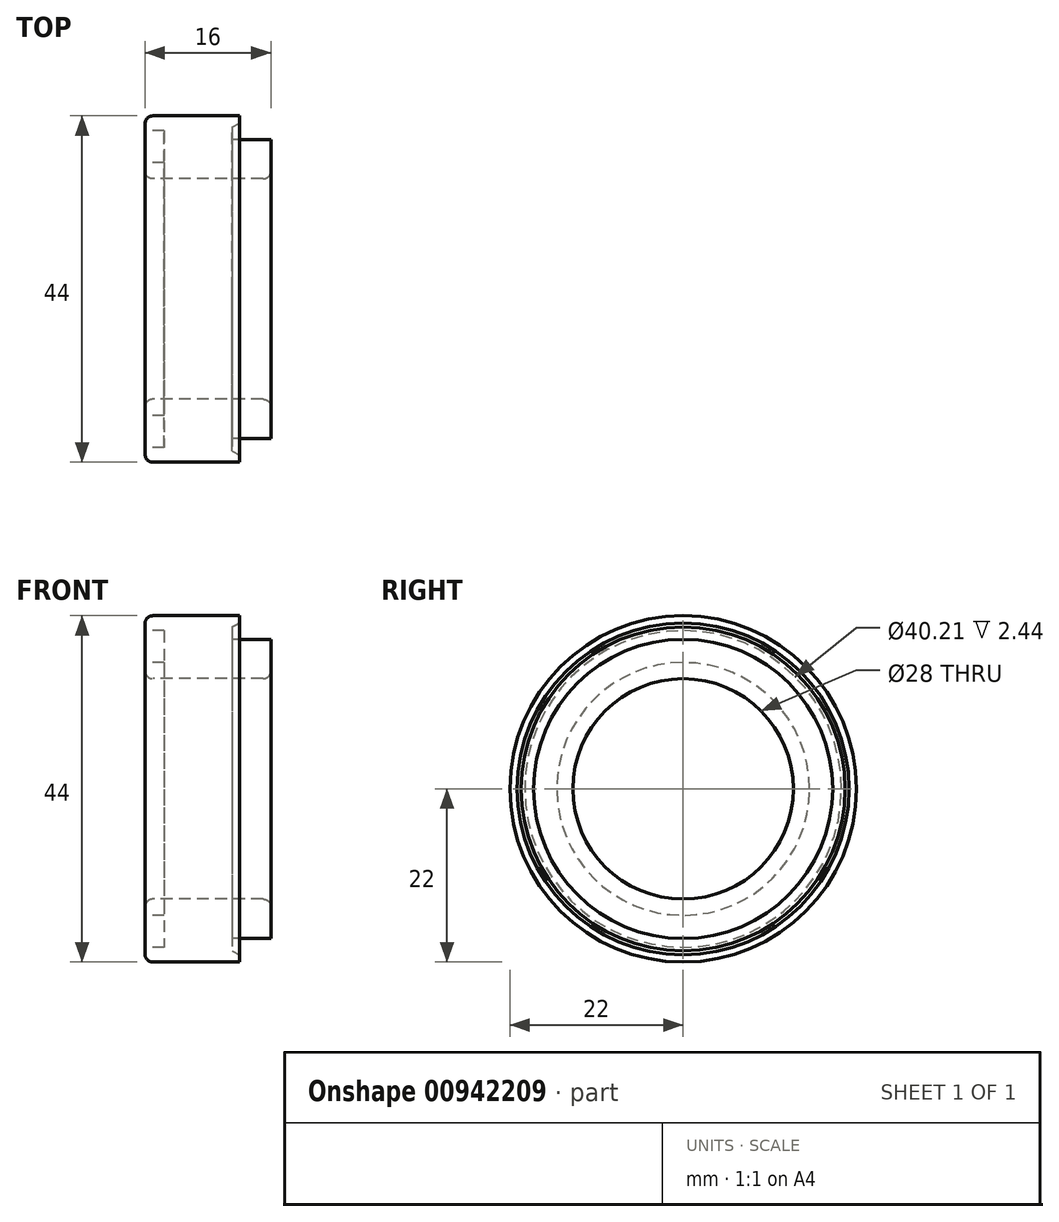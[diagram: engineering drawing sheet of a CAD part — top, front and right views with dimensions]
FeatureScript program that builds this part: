
annotation { "Feature Type Name" : "Feature", "Feature Type Description" : "" }
export const myFeature = defineFeature(function(context is Context, id is Id, definition is map)
    precondition{}
    {
        {
            var Q0;
            Q0=qCreatedBy(makeId("Front.planeOp"),FACE);
            var sketch = newSketch(context, id + "F0", { "sketchPlane" : qUnion([Q0])});
            skLineSegment(sketch, "E0", {"start": v(1, 22) * mm, "end": v(12, 22) * mm});
            skLineSegment(sketch, "E1", {"start": v(1, 14) * mm, "end": v(15, 14) * mm});
            skLineSegment(sketch, "E2", {"start": v(16, 15) * mm, "end": v(16, 19) * mm});
            skLineSegment(sketch, "E3", {"start": v(16, 19) * mm, "end": v(12, 19) * mm});
            skLineSegment(sketch, "E4", {"start": v(12, 21.08) * mm, "end": v(12, 22) * mm});
            skLineSegment(sketch, "E5", {"start": v(0, 0) * mm, "end": v(23.78, 0) * mm});
            skLineSegment(sketch, "E6", {"start": v(0, 15) * mm, "end": v(0, 16.06) * mm});
            skPoint(sketch, "E7.visualSharp", {"position": v(0, 22) * mm});
            skArc(sketch, "E7.filletArc", {"start": v(1, 22) * mm, "mid": v(0.3, 21.7) * mm, "end": v(0, 21) * mm});
            skPoint(sketch, "E8.visualSharp", {"position": v(0, 14) * mm});
            skArc(sketch, "E8.filletArc", {"start": v(0, 15) * mm, "mid": v(0.3, 14.3) * mm, "end": v(1, 14) * mm});
            skPoint(sketch, "E9.visualSharp", {"position": v(16, 14) * mm});
            skArc(sketch, "E9.filletArc", {"start": v(15, 14) * mm, "mid": v(15.7, 14.3) * mm, "end": v(16, 15) * mm});
            skLineSegment(sketch, "E10", {"start": v(0, 20.1) * mm, "end": v(2.44, 20.1) * mm});
            skLineSegment(sketch, "E11", {"start": v(2.44, 20.1) * mm, "end": v(2.44, 16.06) * mm});
            skLineSegment(sketch, "E12", {"start": v(2.44, 16.06) * mm, "end": v(0, 16.06) * mm});
            skLineSegment(sketch, "E13.trimOffspring", {"start": v(0, 20.1) * mm, "end": v(0, 21) * mm});
            skLineSegment(sketch, "E14", {"start": v(12, 21.08) * mm, "end": v(11.04, 20.57) * mm});
            skLineSegment(sketch, "E15", {"start": v(11.04, 20.57) * mm, "end": v(11.04, 19) * mm});
            skLineSegment(sketch, "E16", {"start": v(11.04, 19) * mm, "end": v(12, 19) * mm});
            skSolve(sketch);
        }
        {
            var Q0;
            Q0=makeQuery(id+"F0.imprint","IMPRINT",FACE,{"disambiguationData":[TD([[makeQuery(id+"F0.imprint","IMPRINT",EDGE,{"derivedFrom":sQuery(id+"F0.wireOp",EDGE,"E0")}),-1.0]])]});
            var Q1;
            Q1=sQuery(id+"F0.wireOp",EDGE,"E5");
            revolve(context, id + "F1", {"surfaceOperationType" : NewSurfaceOperationType.NEW, "entities" : qUnion([Q0]), "axis" : qUnion([Q1]), "revolveType" : RevolveType.FULL});
        }
    });
